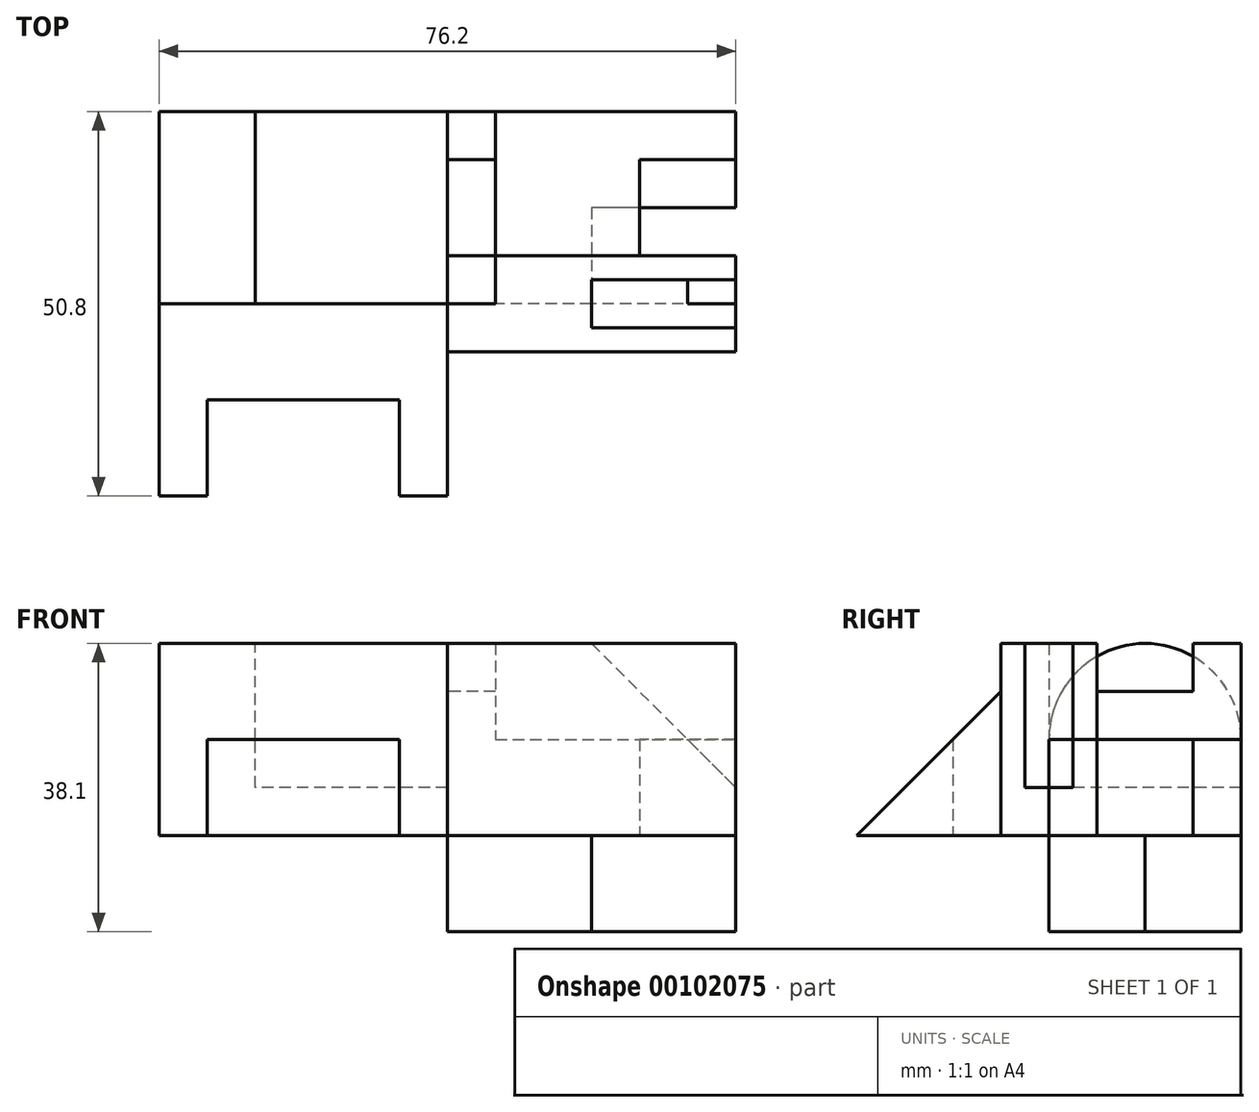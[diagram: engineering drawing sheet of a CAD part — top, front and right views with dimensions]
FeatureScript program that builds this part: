
annotation { "Feature Type Name" : "Feature", "Feature Type Description" : "" }
export const myFeature = defineFeature(function(context is Context, id is Id, definition is map)
    precondition{}
    {
        {
            var Q0;
            Q0=qCreatedBy(makeId("Front.planeOp"),FACE);
            var sketch = newSketch(context, id + "F0", { "sketchPlane" : qUnion([Q0])});
            skLineSegment(sketch, "E0", {"start": v(0, 0) * mm, "end": v(0, 25.4) * mm});
            skLineSegment(sketch, "E1", {"start": v(0, 25.4) * mm, "end": v(6.35, 25.4) * mm});
            skLineSegment(sketch, "E2", {"start": v(6.35, 25.4) * mm, "end": v(6.35, 12.7) * mm});
            skLineSegment(sketch, "E3", {"start": v(6.35, 12.7) * mm, "end": v(38.1, 12.7) * mm});
            skLineSegment(sketch, "E4", {"start": v(38.1, 12.7) * mm, "end": v(38.1, 0) * mm});
            skLineSegment(sketch, "E5", {"start": v(38.1, 0) * mm, "end": v(0, 0) * mm});
            skSolve(sketch);
        }
        {
            var Q0;
            Q0=makeQuery(id+"F0.imprint","IMPRINT",FACE,{"disambiguationData":[TD([[makeQuery(id+"F0.imprint","IMPRINT",EDGE,{"derivedFrom":sQuery(id+"F0.wireOp",EDGE,"E0")}),-1.0]])]});
            extrude(context, id + "F1", {"entities" : qUnion([Q0]), "oppositeDirection" : true, "depth" : 25.4 * mm});
        }
        {
            var Q0;
            Q0=qCreatedBy(makeId("Top.planeOp"),FACE);
            var sketch = newSketch(context, id + "F2", { "sketchPlane" : qUnion([Q0])});
            skLineSegment(sketch, "E6", {"start": v(0, 0) * mm, "end": v(0, 25.4) * mm});
            skLineSegment(sketch, "E7", {"start": v(0, 25.4) * mm, "end": v(38.1, 25.4) * mm});
            skLineSegment(sketch, "E8", {"start": v(38.1, 25.4) * mm, "end": v(38.1, 12.7) * mm});
            skLineSegment(sketch, "E9", {"start": v(38.1, 12.7) * mm, "end": v(19.05, 12.7) * mm});
            skLineSegment(sketch, "E10", {"start": v(19.05, 12.7) * mm, "end": v(19.05, 0) * mm});
            skLineSegment(sketch, "E11", {"start": v(19.05, 0) * mm, "end": v(0, 0) * mm});
            skSolve(sketch);
        }
        {
            var Q0;
            Q0=makeQuery(id+"F2.imprint","IMPRINT",FACE,{"disambiguationData":[TD([[makeQuery(id+"F2.imprint","IMPRINT",EDGE,{"derivedFrom":sQuery(id+"F2.wireOp",EDGE,"E6")}),-1.0]])]});
            extrude(context, id + "F3", {"entities" : qUnion([Q0]), "oppositeDirection" : true, "depth" : 12.7 * mm});
        }
        {
            var Q0;
            Q0=makeQuery(id+"F3.opExtrude","CAP_FACE",FACE,{"disambiguationData":[OSD([sQuery(id+"F2.wireOp",EDGE,"E6"),sQuery(id+"F2.wireOp",EDGE,"E7"),sQuery(id+"F2.wireOp",EDGE,"E8"),sQuery(id+"F2.wireOp",EDGE,"E9"),sQuery(id+"F2.wireOp",EDGE,"E10"),sQuery(id+"F2.wireOp",EDGE,"E11")])],"isStart":true});
            var sketch = newSketch(context, id + "F4", { "sketchPlane" : qUnion([Q0])});
            skLineSegment(sketch, "E12.bottom", {"start": v(0, 25.4) * mm, "end": v(6.35, 25.4) * mm});
            skLineSegment(sketch, "E12.top", {"start": v(0, 6.35) * mm, "end": v(6.35, 6.35) * mm});
            skLineSegment(sketch, "E12.left", {"start": v(0, 25.4) * mm, "end": v(0, 6.35) * mm});
            skLineSegment(sketch, "E12.right", {"start": v(6.35, 25.4) * mm, "end": v(6.35, 6.35) * mm});
            skSolve(sketch);
        }
        {
            var Q0;
            Q0=makeQuery(id+"F4.imprint","IMPRINT",FACE,{"disambiguationData":[TD([[makeQuery(id+"F4.imprint","IMPRINT",EDGE,{"derivedFrom":sQuery(id+"F4.wireOp",EDGE,"E12.bottom")}),-1.0]])]});
            extrude(context, id + "F5", {"entities" : qUnion([Q0]), "operationType" : NewBodyOperationType.ADD, "depth" : 12.7 * mm});
        }
        {
            var Q0;
            Q0=qCreatedBy(makeId("Front.planeOp"),FACE);
            var sketch = newSketch(context, id + "F6", { "sketchPlane" : qUnion([Q0])});
            skLineSegment(sketch, "E13", {"start": v(0, 0) * mm, "end": v(0, 25.4) * mm});
            skLineSegment(sketch, "E14", {"start": v(0, 25.4) * mm, "end": v(6.35, 25.4) * mm});
            skLineSegment(sketch, "E15", {"start": v(6.35, 25.4) * mm, "end": v(6.35, 12.7) * mm});
            skLineSegment(sketch, "E16", {"start": v(6.35, 12.7) * mm, "end": v(38.1, 12.7) * mm});
            skLineSegment(sketch, "E17", {"start": v(38.1, 12.7) * mm, "end": v(38.1, 0) * mm});
            skLineSegment(sketch, "E18", {"start": v(38.1, 0) * mm, "end": v(0, 0) * mm});
            skSolve(sketch);
        }
        {
            var Q0;
            Q0=makeQuery(id+"F6.imprint","IMPRINT",FACE,{"disambiguationData":[TD([[makeQuery(id+"F6.imprint","IMPRINT",EDGE,{"derivedFrom":sQuery(id+"F6.wireOp",EDGE,"E13")}),-1.0]])]});
            extrude(context, id + "F7", {"entities" : qUnion([Q0]), "oppositeDirection" : true, "depth" : 25.4 * mm});
        }
        {
            var Q0;
            Q0=makeQuery(id+"F7.opExtrude","SWEPT_FACE",FACE,{"disambiguationData":[OSD([sQuery(id+"F6.wireOp",EDGE,"E13")])]});
            var sketch = newSketch(context, id + "F8", { "sketchPlane" : qUnion([Q0])});
            skLineSegment(sketch, "E19.bottom", {"start": v(-19.05, 25.4) * mm, "end": v(-6.35, 25.4) * mm});
            skLineSegment(sketch, "E19.top", {"start": v(-19.05, 19.05) * mm, "end": v(-6.35, 19.05) * mm});
            skLineSegment(sketch, "E19.left", {"start": v(-19.05, 25.4) * mm, "end": v(-19.05, 19.05) * mm});
            skLineSegment(sketch, "E19.right", {"start": v(-6.35, 25.4) * mm, "end": v(-6.35, 19.05) * mm});
            skSolve(sketch);
        }
        {
            var Q0;
            Q0 = qSketchRegion(id + "F8", true);
            extrude(context, id + "F9", {"entities" : qUnion([Q0]), "operationType" : NewBodyOperationType.REMOVE, "endBound" : BoundingType.THROUGH_ALL, "oppositeDirection" : true, "depth" : 25.4 * mm});
        }
        {
            var Q0;
            Q0=makeQuery(id+"F7.opExtrude","SWEPT_FACE",FACE,{"disambiguationData":[OSD([sQuery(id+"F6.wireOp",EDGE,"E18")])]});
            var sketch = newSketch(context, id + "F10", { "sketchPlane" : qUnion([Q0])});
            skLineSegment(sketch, "E20.bottom", {"start": v(38.1, -6.35) * mm, "end": v(25.4, -6.35) * mm});
            skLineSegment(sketch, "E20.top", {"start": v(38.1, -19.05) * mm, "end": v(25.4, -19.05) * mm});
            skLineSegment(sketch, "E20.left", {"start": v(38.1, -6.35) * mm, "end": v(38.1, -19.05) * mm});
            skLineSegment(sketch, "E20.right", {"start": v(25.4, -6.35) * mm, "end": v(25.4, -19.05) * mm});
            skSolve(sketch);
        }
        {
            var Q0;
            Q0=makeQuery(id+"F10.imprint","IMPRINT",FACE,{"disambiguationData":[TD([[makeQuery(id+"F10.imprint","IMPRINT",EDGE,{"derivedFrom":sQuery(id+"F10.wireOp",EDGE,"E20.bottom")}),1.0]])]});
            extrude(context, id + "F11", {"entities" : qUnion([Q0]), "operationType" : NewBodyOperationType.REMOVE, "endBound" : BoundingType.THROUGH_ALL, "oppositeDirection" : true, "depth" : 25.4 * mm});
        }
        {
            var Q0;
            Q0=qCreatedBy(makeId("Front.planeOp"),FACE);
            var sketch = newSketch(context, id + "F12", { "sketchPlane" : qUnion([Q0])});
            skLineSegment(sketch, "E21", {"start": v(0, 0) * mm, "end": v(0, 25.4) * mm});
            skLineSegment(sketch, "E22", {"start": v(0, 25.4) * mm, "end": v(38.1, 25.4) * mm});
            skLineSegment(sketch, "E23", {"start": v(38.1, 25.4) * mm, "end": v(38.1, 0) * mm});
            skLineSegment(sketch, "E24", {"start": v(38.1, 0) * mm, "end": v(0, 0) * mm});
            skSolve(sketch);
        }
        {
            var Q0;
            Q0=makeQuery(id+"F12.imprint","IMPRINT",FACE,{"disambiguationData":[TD([[makeQuery(id+"F12.imprint","IMPRINT",EDGE,{"derivedFrom":sQuery(id+"F12.wireOp",EDGE,"E21")}),-1.0]])]});
            extrude(context, id + "F13", {"entities" : qUnion([Q0]), "endBound" : BoundingType.SYMMETRIC, "oppositeDirection" : true, "depth" : 12.7 * mm});
        }
        {
            var Q0;
            Q0=qCreatedBy(makeId("Front.planeOp"),FACE);
            var sketch = newSketch(context, id + "F14", { "sketchPlane" : qUnion([Q0])});
            skLineSegment(sketch, "E25", {"start": v(38.1, 25.4) * mm, "end": v(19.05, 25.4) * mm});
            skLineSegment(sketch, "E26", {"start": v(19.05, 25.4) * mm, "end": v(38.1, 6.35) * mm});
            skLineSegment(sketch, "E27", {"start": v(38.1, 6.35) * mm, "end": v(38.1, 25.4) * mm});
            skSolve(sketch);
        }
        {
            var Q0;
            Q0 = qSketchRegion(id + "F14", true);
            extrude(context, id + "F15", {"entities" : qUnion([Q0]), "operationType" : NewBodyOperationType.REMOVE, "endBound" : BoundingType.SYMMETRIC, "oppositeDirection" : true, "depth" : 6.35 * mm});
        }
        {
            var Q0;
            Q0=qCreatedBy(makeId("Right.planeOp"),FACE);
            var sketch = newSketch(context, id + "F16", { "sketchPlane" : qUnion([Q0])});
            skLineSegment(sketch, "E28", {"start": v(0, 0) * mm, "end": v(-25.4, 0) * mm});
            skLineSegment(sketch, "E29", {"start": v(-25.4, 0) * mm, "end": v(0, 25.4) * mm});
            skLineSegment(sketch, "E30", {"start": v(0, 25.4) * mm, "end": v(0, 0) * mm});
            skSolve(sketch);
        }
        {
            var Q0;
            Q0=makeQuery(id+"F16.imprint","IMPRINT",FACE,{"disambiguationData":[TD([[makeQuery(id+"F16.imprint","IMPRINT",EDGE,{"derivedFrom":sQuery(id+"F16.wireOp",EDGE,"E28")}),-1.0]])]});
            extrude(context, id + "F17", {"entities" : qUnion([Q0]), "oppositeDirection" : true, "depth" : 38.1 * mm});
        }
        {
            var Q0;
            Q0=makeQuery(id+"F17.opExtrude","SWEPT_FACE",FACE,{"disambiguationData":[OSD([sQuery(id+"F16.wireOp",EDGE,"E28")])]});
            var sketch = newSketch(context, id + "F18", { "sketchPlane" : qUnion([Q0])});
            skLineSegment(sketch, "E31.bottom", {"start": v(-31.75, 25.4) * mm, "end": v(-6.35, 25.4) * mm});
            skLineSegment(sketch, "E31.top", {"start": v(-31.75, 12.7) * mm, "end": v(-6.35, 12.7) * mm});
            skLineSegment(sketch, "E31.left", {"start": v(-31.75, 25.4) * mm, "end": v(-31.75, 12.7) * mm});
            skLineSegment(sketch, "E31.right", {"start": v(-6.35, 25.4) * mm, "end": v(-6.35, 12.7) * mm});
            skSolve(sketch);
        }
        {
            var Q0;
            Q0 = qSketchRegion(id + "F18", true);
            extrude(context, id + "F19", {"entities" : qUnion([Q0]), "operationType" : NewBodyOperationType.REMOVE, "endBound" : BoundingType.THROUGH_ALL, "oppositeDirection" : true, "depth" : 25.4 * mm});
        }
        {
            var Q0;
            Q0=qCreatedBy(makeId("Front.planeOp"),FACE);
            var sketch = newSketch(context, id + "F20", { "sketchPlane" : qUnion([Q0])});
            skLineSegment(sketch, "E32", {"start": v(0, 0) * mm, "end": v(-38.1, 0) * mm});
            skLineSegment(sketch, "E33", {"start": v(-38.1, 0) * mm, "end": v(-38.1, 12.7) * mm});
            skLineSegment(sketch, "E34", {"start": v(0, 0) * mm, "end": v(0, 6.35) * mm});
            skLineSegment(sketch, "E35", {"start": v(0, 6.35) * mm, "end": v(-25.4, 6.35) * mm});
            skLineSegment(sketch, "E36", {"start": v(-25.4, 6.35) * mm, "end": v(-25.4, 12.7) * mm});
            skLineSegment(sketch, "E37", {"start": v(-25.4, 12.7) * mm, "end": v(-38.1, 12.7) * mm});
            skSolve(sketch);
        }
        {
            var Q0;
            Q0=makeQuery(id+"F20.imprint","IMPRINT",FACE,{"disambiguationData":[TD([[makeQuery(id+"F20.imprint","IMPRINT",EDGE,{"derivedFrom":sQuery(id+"F20.wireOp",EDGE,"E32")}),-1.0]])]});
            extrude(context, id + "F21", {"entities" : qUnion([Q0]), "oppositeDirection" : true, "depth" : 25.4 * mm});
        }
        {
            var Q0;
            Q0=makeQuery(id+"F21.opExtrude","SWEPT_FACE",FACE,{"disambiguationData":[OSD([sQuery(id+"F20.wireOp",EDGE,"E36")])]});
            var sketch = newSketch(context, id + "F22", { "sketchPlane" : qUnion([Q0])});
            skArc(sketch, "E38", {"start": v(25.4, 12.7) * mm, "mid": v(12.7, 25.4) * mm, "end": v(0, 12.7) * mm});
            skSolve(sketch);
        }
        {
            var Q0;
            Q0=makeQuery(id+"F22.imprint","IMPRINT",FACE,{"disambiguationData":[TD([[makeQuery(id+"F22.imprint","IMPRINT",EDGE,{"derivedFrom":sQuery(id+"F22.wireOp",EDGE,"E38")}),1.0]])]});
            extrude(context, id + "F23", {"entities" : qUnion([Q0]), "operationType" : NewBodyOperationType.ADD, "oppositeDirection" : true, "depth" : 12.7 * mm});
        }
    });
